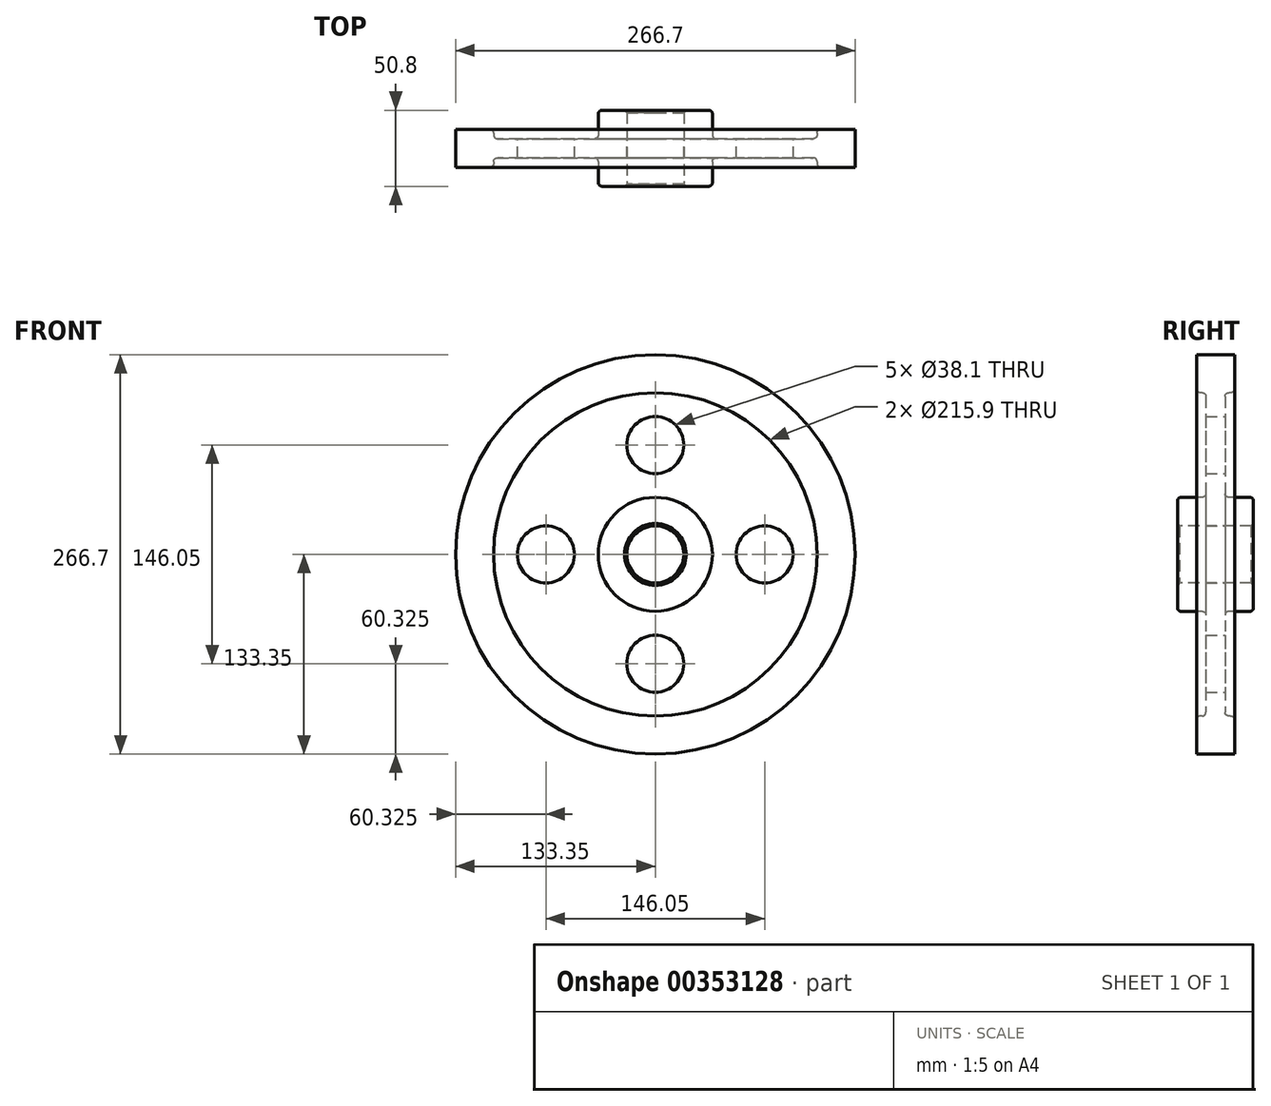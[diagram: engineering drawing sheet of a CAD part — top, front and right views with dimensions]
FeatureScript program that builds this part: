
annotation { "Feature Type Name" : "Feature", "Feature Type Description" : "" }
export const myFeature = defineFeature(function(context is Context, id is Id, definition is map)
    precondition{}
    {
        {
            var Q0;
            Q0=qCreatedBy(makeId("Right.planeOp"),FACE);
            var sketch = newSketch(context, id + "F0", { "sketchPlane" : qUnion([Q0])});
            skLineSegment(sketch, "E0", {"start": v(0, 0) * mm, "end": v(76.8, 0) * mm, "construction": true});
            skLineSegment(sketch, "E1.0", {"start": v(0, 19.05) * mm, "end": v(25.4, 19.05) * mm});
            skLineSegment(sketch, "E2.0", {"start": v(6.35, 107.95) * mm, "end": v(12.7, 107.95) * mm});
            skLineSegment(sketch, "E3.0", {"start": v(0, 133.35) * mm, "end": v(12.7, 133.35) * mm});
            skLineSegment(sketch, "E4", {"start": v(0, 133.35) * mm, "end": v(0, 0) * mm, "construction": true});
            skLineSegment(sketch, "E5.0", {"start": v(25.4, 38.1) * mm, "end": v(25.4, 19.05) * mm, "construction": true});
            skLineSegment(sketch, "E6.0", {"start": v(25.4, 38.1) * mm, "end": v(25.4, 19.05) * mm});
            skLineSegment(sketch, "E7.0", {"start": v(6.35, 38.1) * mm, "end": v(25.4, 38.1) * mm});
            skLineSegment(sketch, "E8.0", {"start": v(6.35, 107.95) * mm, "end": v(6.35, 38.1) * mm});
            skLineSegment(sketch, "E9.0", {"start": v(12.7, 133.35) * mm, "end": v(12.7, 107.95) * mm});
            skLineSegment(sketch, "E10.MirrorCS", {"start": v(0, 133.35) * mm, "end": v(-12.7, 133.35) * mm});
            skLineSegment(sketch, "E11.MirrorCS", {"start": v(-12.7, 133.35) * mm, "end": v(-12.7, 107.95) * mm});
            skLineSegment(sketch, "E12.MirrorCS", {"start": v(-6.35, 107.95) * mm, "end": v(-6.35, 38.1) * mm});
            skLineSegment(sketch, "E13.MirrorCS", {"start": v(-6.35, 107.95) * mm, "end": v(-12.7, 107.95) * mm});
            skLineSegment(sketch, "E14.MirrorCS", {"start": v(-6.35, 38.1) * mm, "end": v(-25.4, 38.1) * mm});
            skLineSegment(sketch, "E15.MirrorCS", {"start": v(-25.4, 38.1) * mm, "end": v(-25.4, 19.05) * mm});
            skLineSegment(sketch, "E16.MirrorCS", {"start": v(0, 19.05) * mm, "end": v(-25.4, 19.05) * mm});
            skSolve(sketch);
        }
        {
            var Q0;
            Q0=makeQuery(id+"F0.imprint","IMPRINT",FACE,{"disambiguationData":[TD([[makeQuery(id+"F0.imprint","IMPRINT",EDGE,{"derivedFrom":sQuery(id+"F0.wireOp",EDGE,"E1.0")}),1.0]])]});
            var Q1;
            Q1=sQuery(id+"F0.wireOp",EDGE,"E0");
            revolve(context, id + "F1", {"entities" : qUnion([Q0]), "axis" : qUnion([Q1]), "revolveType" : RevolveType.FULL});
        }
        {
            var Q0;
            Q0=makeQuery(id+"F1.opRevolve","SWEPT_FACE",FACE,{"disambiguationData":[OSD([sQuery(id+"F0.wireOp",EDGE,"E8.0")])]});
            var sketch = newSketch(context, id + "F2", { "sketchPlane" : qUnion([Q0])});
            skLineSegment(sketch, "E17", {"start": v(0, 0) * mm, "end": v(0, 73.03) * mm});
            skCircle(sketch, "E18", {"center": v(0, 73.03) * mm, "radius": 19.05 * mm});
            skCircle(sketch, "E19.1.0", {"center": v(-73.03, 0) * mm, "radius": 19.05 * mm});
            skCircle(sketch, "E19.2.0", {"center": v(0, -73.03) * mm, "radius": 19.05 * mm});
            skCircle(sketch, "E19.3.0", {"center": v(73.03, 0) * mm, "radius": 19.05 * mm});
            skPoint(sketch, "E19.center", {"position": v(0, 0) * mm});
            skSolve(sketch);
        }
        {
            var Q0;
            Q0=makeQuery(id+"F2.imprint","IMPRINT",FACE,{"disambiguationData":[TD([[makeQuery(id+"F2.imprint","IMPRINT",EDGE,{"derivedFrom":sQuery(id+"F2.wireOp",EDGE,"E18")}),1.0]])]});
            var Q1;
            Q1=makeQuery(id+"F2.imprint","IMPRINT",FACE,{"disambiguationData":[TD([[makeQuery(id+"F2.imprint","IMPRINT",EDGE,{"derivedFrom":sQuery(id+"F2.wireOp",EDGE,"E19.3.0")}),1.0]])]});
            var Q2;
            Q2=makeQuery(id+"F2.imprint","IMPRINT",FACE,{"disambiguationData":[TD([[makeQuery(id+"F2.imprint","IMPRINT",EDGE,{"derivedFrom":sQuery(id+"F2.wireOp",EDGE,"E19.1.0")}),1.0]])]});
            var Q3;
            Q3=makeQuery(id+"F2.imprint","IMPRINT",FACE,{"disambiguationData":[TD([[makeQuery(id+"F2.imprint","IMPRINT",EDGE,{"derivedFrom":sQuery(id+"F2.wireOp",EDGE,"E19.2.0")}),1.0]])]});
            extrude(context, id + "F3", {"entities" : qUnion([Q0, Q1, Q2, Q3]), "operationType" : NewBodyOperationType.REMOVE, "oppositeDirection" : true, "depth" : 25.4 * mm});
        }
        {
            var Q0;
            Q0=makeQuery(id+"F1.opRevolve","SWEPT_EDGE",EDGE,{"disambiguationData":[OSD([sQuery(id+"F0.wireOp",EDGE,"E12.MirrorCS"),sQuery(id+"F0.wireOp",EDGE,"E13.MirrorCS")])]});
            var Q1;
            Q1=makeQuery(id+"F1.opRevolve","SWEPT_EDGE",EDGE,{"disambiguationData":[OSD([sQuery(id+"F0.wireOp",EDGE,"E14.MirrorCS"),sQuery(id+"F0.wireOp",EDGE,"E15.MirrorCS")])]});
            var Q2;
            Q2=makeQuery(id+"F1.opRevolve","SWEPT_EDGE",EDGE,{"disambiguationData":[OSD([sQuery(id+"F0.wireOp",EDGE,"E12.MirrorCS"),sQuery(id+"F0.wireOp",EDGE,"E14.MirrorCS")])]});
            var Q3;
            Q3=makeQuery(id+"F1.opRevolve","SWEPT_EDGE",EDGE,{"disambiguationData":[OSD([sQuery(id+"F0.wireOp",EDGE,"E11.MirrorCS"),sQuery(id+"F0.wireOp",EDGE,"E13.MirrorCS")])]});
            var Q4;
            Q4=makeQuery(id+"F1.opRevolve","SWEPT_EDGE",EDGE,{"disambiguationData":[OSD([sQuery(id+"F0.wireOp",EDGE,"E2.0"),sQuery(id+"F0.wireOp",EDGE,"E9.0")])]});
            var Q5;
            Q5=makeQuery(id+"F1.opRevolve","SWEPT_EDGE",EDGE,{"disambiguationData":[OSD([sQuery(id+"F0.wireOp",EDGE,"E2.0"),sQuery(id+"F0.wireOp",EDGE,"E8.0")])]});
            var Q6;
            Q6=makeQuery(id+"F1.opRevolve","SWEPT_EDGE",EDGE,{"disambiguationData":[OSD([sQuery(id+"F0.wireOp",EDGE,"E6.0"),sQuery(id+"F0.wireOp",EDGE,"E7.0")])]});
            var Q7;
            Q7=makeQuery(id+"F1.opRevolve","SWEPT_EDGE",EDGE,{"disambiguationData":[OSD([sQuery(id+"F0.wireOp",EDGE,"E7.0"),sQuery(id+"F0.wireOp",EDGE,"E8.0")])]});
            fillet(context, id + "F4", {"entities" : qUnion([Q0, Q1, Q2, Q3, Q4, Q5, Q6, Q7]), "radius" : 2.54 * mm, "tangentPropagation" : true, "allowEdgeOverflow" : false});
        }
        {
            var Q0;
            Q0=makeQuery(id+"F1.opRevolve","SWEPT_EDGE",EDGE,{"disambiguationData":[OSD([sQuery(id+"F0.wireOp",EDGE,"E15.MirrorCS"),sQuery(id+"F0.wireOp",EDGE,"E16.MirrorCS")])]});
            var Q1;
            Q1=makeQuery(id+"F1.opRevolve","SWEPT_EDGE",EDGE,{"disambiguationData":[OSD([sQuery(id+"F0.wireOp",EDGE,"E1.0"),sQuery(id+"F0.wireOp",EDGE,"E6.0")])]});
            chamfer(context, id + "F5", {"entities" : qUnion([Q0, Q1]), "width" : 1.59 * mm, "tangentPropagation" : true});
        }
    });
